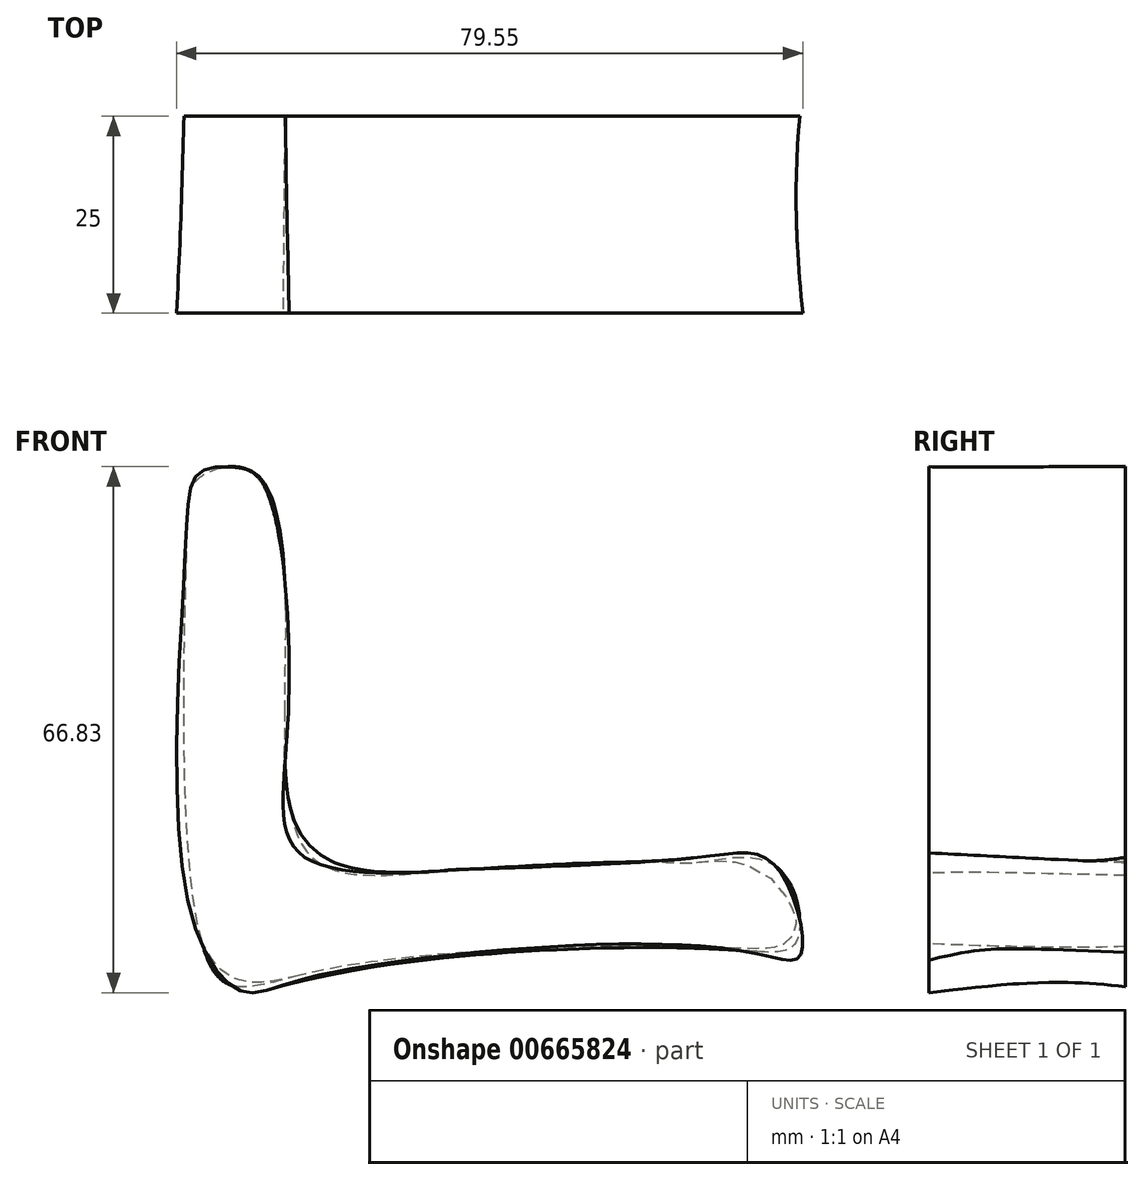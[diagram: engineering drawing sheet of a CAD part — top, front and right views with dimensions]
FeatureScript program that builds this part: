
annotation { "Feature Type Name" : "Feature", "Feature Type Description" : "" }
export const myFeature = defineFeature(function(context is Context, id is Id, definition is map)
    precondition{}
    {
        {
            var Q0;
            Q0=qCreatedBy(makeId("Front.planeOp"),FACE);
            var sketch = newSketch(context, id + "F0", { "sketchPlane" : qUnion([Q0])});
            skFitSpline(sketch, "E0", {"points": [v(-46.14, 44.64) * mm, v(-44.26, 52.16) * mm, v(-36.93, 51.97) * mm, v(-33.74, 27.53) * mm, v(-33.74, 20.4) * mm, v(-30.92, 4.42) * mm, v(-12.69, 1.97) * mm, v(14.2, 3.1) * mm, v(18.89, 3.1) * mm, v(28.66, 2.54) * mm, v(31.3, -6.86) * mm, v(22.65, -7.99) * mm, v(-29.79, -10.8) * mm, v(-42.95, -10.43) * mm, v(-46.14, 44.64) * mm]});
            skSolve(sketch);
        }
        {
            var Q0;
            Q0=qCreatedBy(makeId("Front.planeOp"),FACE);
            cPlane(context, id + "F1", {"entities" : qUnion([Q0]), "cplaneType" : CPlaneType.OFFSET, "offset" : 25 * mm, "width" : 150 * mm, "height" : 150 * mm});
        }
        {
            var Q0;
            Q0=qCreatedBy(id+"F1.planeOp",FACE);
            var sketch = newSketch(context, id + "F2", { "sketchPlane" : qUnion([Q0])});
            skFitSpline(sketch, "E1", {"points": [v(-40.5, 53.28) * mm, v(-44.64, 52.53) * mm, v(-46.33, 43.13) * mm, v(-46.14, -1.4) * mm, v(-39.38, -13.25) * mm, v(-30.54, -11.56) * mm, v(23.21, -7.99) * mm, v(31.86, -8.55) * mm, v(28.66, 2.54) * mm, v(18.51, 3.66) * mm, v(-11.37, 2.16) * mm, v(-14.2, 1.97) * mm, v(-31.1, 3.66) * mm, v(-33.36, 20.4) * mm, v(-36.56, 51.22) * mm, v(-40.5, 53.28) * mm]});
            skSolve(sketch);
        }
        {
            var Q0;
            Q0=makeQuery(id+"F2.imprint","IMPRINT",FACE,{"disambiguationData":[TD([[makeQuery(id+"F2.imprint","IMPRINT",EDGE,{"derivedFrom":sQuery(id+"F2.wireOp",EDGE,"E1")}),1.0]])]});
            var Q1;
            Q1=makeQuery(id+"F0.imprint","IMPRINT",FACE,{"disambiguationData":[TD([[makeQuery(id+"F0.imprint","IMPRINT",EDGE,{"derivedFrom":sQuery(id+"F0.wireOp",EDGE,"E0")}),-1.0]])]});
            loft(context, id + "F3", {"sheetProfilesArray" : [{ "sheetProfileEntities" : qUnion([Q0]) }, { "sheetProfileEntities" : qUnion([Q1]) }]});
        }
    });
